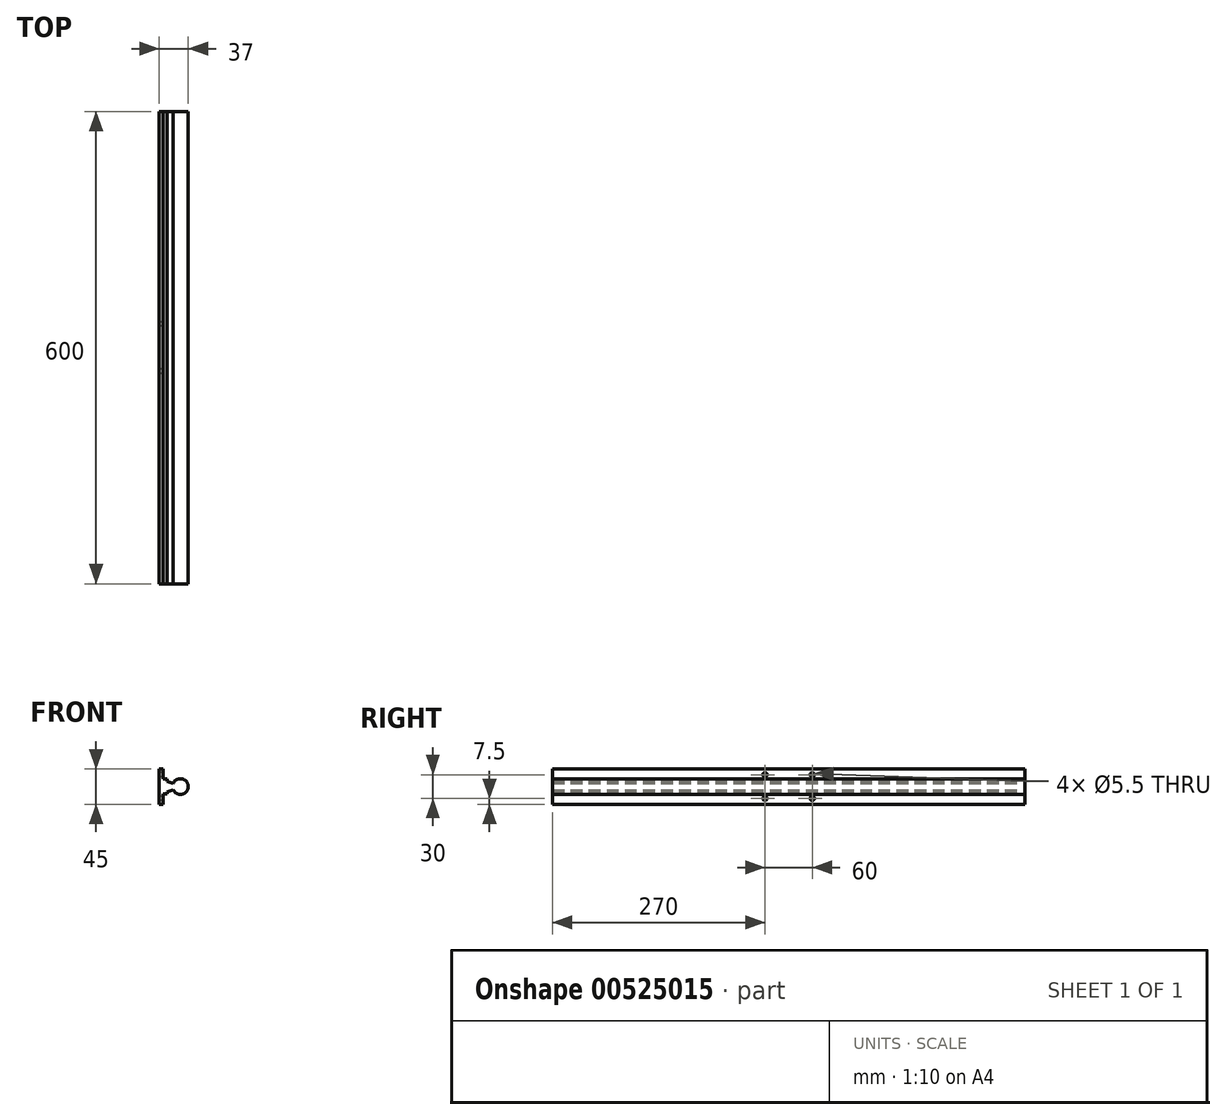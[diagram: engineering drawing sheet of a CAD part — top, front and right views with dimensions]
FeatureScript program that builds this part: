
annotation { "Feature Type Name" : "Feature", "Feature Type Description" : "" }
export const myFeature = defineFeature(function(context is Context, id is Id, definition is map)
    precondition{}
    {
        {
            var Q0;
            Q0=qCreatedBy(makeId("Front.planeOp"),FACE);
            var sketch = newSketch(context, id + "F0", { "sketchPlane" : qUnion([Q0])});
            skLineSegment(sketch, "E0.bottom", {"start": v(0, 22.5) * mm, "end": v(5, 22.5) * mm});
            skLineSegment(sketch, "E0.top", {"start": v(0, -22.5) * mm, "end": v(5, -22.5) * mm});
            skLineSegment(sketch, "E0.left", {"start": v(0, 22.5) * mm, "end": v(0, -22.5) * mm});
            skLineSegment(sketch, "E0.right", {"start": v(5, 22.5) * mm, "end": v(5, 9.5) * mm});
            skLineSegment(sketch, "E1.bottom", {"start": v(5, 9.5) * mm, "end": v(10, 9.5) * mm});
            skLineSegment(sketch, "E1.top", {"start": v(5, -9.5) * mm, "end": v(10, -9.5) * mm});
            skLineSegment(sketch, "E1.right", {"start": v(10, 9.5) * mm, "end": v(10, 6.38) * mm});
            skLineSegment(sketch, "E2", {"start": v(10, 6.38) * mm, "end": v(17.89, 4.12) * mm});
            skLineSegment(sketch, "E3", {"start": v(17.92, -4.2) * mm, "end": v(10, -6.5) * mm});
            skArc(sketch, "E4", {"start": v(17.92, -4.2) * mm, "mid": v(37, 0.04) * mm, "end": v(17.89, 4.12) * mm});
            skLineSegment(sketch, "E5.trimOffspring", {"start": v(5, -9.5) * mm, "end": v(5, -22.5) * mm});
            skLineSegment(sketch, "E6.trimOffspring", {"start": v(10, -6.5) * mm, "end": v(10, -9.5) * mm});
            skPoint(sketch, "E7.orphan", {"position": v(32.3, 0) * mm});
            skSolve(sketch);
        }
        {
            var Q0;
            Q0=qSketchRegion(id+"F0",true);
            extrude(context, id + "F1", {"entities" : qUnion([Q0]), "endBound" : BoundingType.SYMMETRIC, "depth" : 600 * mm, "offsetDistance" : 25 * mm});
        }
        {
            var Q0;
            Q0=makeQuery(id+"F1.opExtrude","SWEPT_FACE",FACE,{"disambiguationData":[OSD([sQuery(id+"F0.wireOp",EDGE,"E0.left")])]});
            var sketch = newSketch(context, id + "F2", { "sketchPlane" : qUnion([Q0])});
            skCircle(sketch, "E8", {"center": v(30, 15) * mm, "radius": 2.75 * mm});
            skCircle(sketch, "E9", {"center": v(30, -15) * mm, "radius": 2.75 * mm});
            skCircle(sketch, "E10", {"center": v(-30, -15) * mm, "radius": 2.75 * mm});
            skCircle(sketch, "E11", {"center": v(-30, 15) * mm, "radius": 2.75 * mm});
            skSolve(sketch);
        }
        {
            var Q0;
            Q0=qSketchRegion(id+"F2",true);
            extrude(context, id + "F3", {"entities" : qUnion([Q0]), "operationType" : NewBodyOperationType.REMOVE, "oppositeDirection" : true, "depth" : 5 * mm, "offsetDistance" : 25 * mm});
        }
    });
